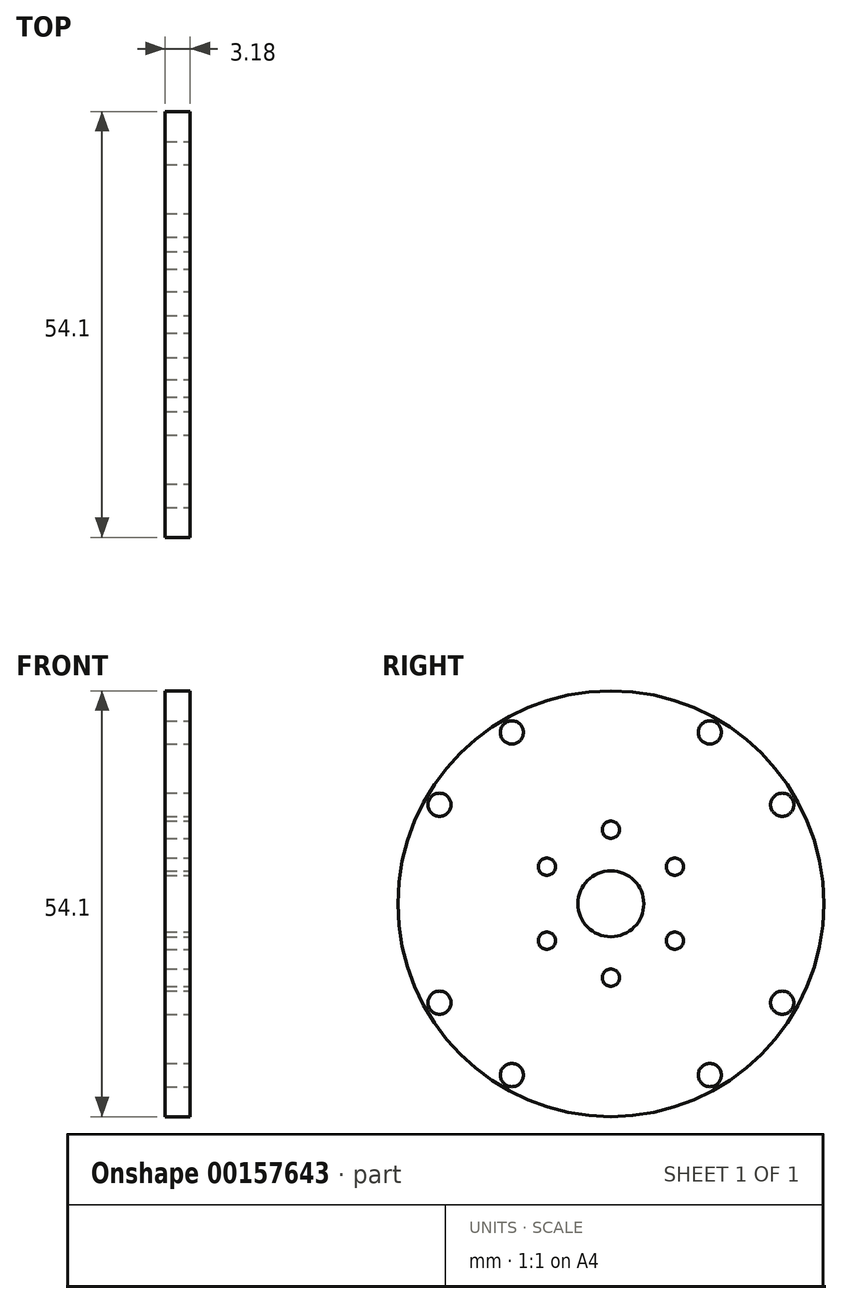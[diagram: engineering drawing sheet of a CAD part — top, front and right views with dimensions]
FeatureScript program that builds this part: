
annotation { "Feature Type Name" : "Feature", "Feature Type Description" : "" }
export const myFeature = defineFeature(function(context is Context, id is Id, definition is map)
    precondition{}
    {
        {
            var Q0;
            Q0=qCreatedBy(makeId("Right.planeOp"),FACE);
            var sketch = newSketch(context, id + "F0", { "sketchPlane" : qUnion([Q0])});
            skCircle(sketch, "E0", {"center": v(0, 0) * mm, "radius": 27.05 * mm});
            skCircle(sketch, "E1", {"center": v(12.57, 21.77) * mm, "radius": 1.47 * mm});
            skCircle(sketch, "E2", {"center": v(21.77, 12.57) * mm, "radius": 1.47 * mm});
            skCircle(sketch, "E3", {"center": v(8.13, 4.7) * mm, "radius": 1.1 * mm});
            skCircle(sketch, "E4", {"center": v(0, 9.4) * mm, "radius": 1.1 * mm});
            skCircle(sketch, "E5.MirrorC", {"center": v(-12.57, 21.77) * mm, "radius": 1.47 * mm});
            skCircle(sketch, "E6.MirrorC", {"center": v(-21.77, 12.57) * mm, "radius": 1.47 * mm});
            skCircle(sketch, "E7.MirrorC", {"center": v(-8.13, 4.7) * mm, "radius": 1.1 * mm});
            skCircle(sketch, "E8.MirrorC", {"center": v(-21.77, -12.57) * mm, "radius": 1.47 * mm});
            skCircle(sketch, "E9.MirrorC", {"center": v(-12.57, -21.77) * mm, "radius": 1.47 * mm});
            skCircle(sketch, "E10.MirrorC", {"center": v(12.57, -21.77) * mm, "radius": 1.47 * mm});
            skCircle(sketch, "E11.MirrorC", {"center": v(21.77, -12.57) * mm, "radius": 1.47 * mm});
            skCircle(sketch, "E12.MirrorC", {"center": v(-8.13, -4.7) * mm, "radius": 1.1 * mm});
            skCircle(sketch, "E13.MirrorC", {"center": v(8.13, -4.7) * mm, "radius": 1.1 * mm});
            skCircle(sketch, "E14.MirrorC", {"center": v(0, -9.4) * mm, "radius": 1.1 * mm});
            skCircle(sketch, "E15", {"center": v(0, 0) * mm, "radius": 4.2 * mm});
            skSolve(sketch);
        }
        {
            var Q0;
            Q0=makeQuery(id+"F0.imprint","IMPRINT",FACE,{"disambiguationData":[TD([[makeQuery(id+"F0.imprint","IMPRINT",EDGE,{"derivedFrom":sQuery(id+"F0.wireOp",EDGE,"E0")}),1.0]])]});
            extrude(context, id + "F1", {"entities" : qUnion([Q0]), "oppositeDirection" : true, "depth" : 3.17 * mm});
        }
    });
